# Revit family: CLEVER_GRIFERIA_GRIFO MURAL JARDÍN
name_source: partatom
category: Aparatos sanitarios
revit_build: Autodesk Revit 2016 (Build: 20151007_0715(x64)
units: mm (PartAtom-declared; Revit-internal decimal feet)

## family parameters
Anfitrión = Cara
Compartido = No
Corte con vacíos al cargar = No
Cota de conector redondo = Diámetro de uso
Número OmniClass = 23.45.05.14.14
Punto de cálculo de habitación = No
Tipo de pieza = Normal
Título OmniClass = Sinks/Lavatories

## types (1)
- Grifos individuales - Grifo mural jardín
    Altura = 100 mm  [stored 0.328084 ft]
    Apertura = Monomando
    BIMETRICAL = http://www.bimetrical.com
    BIMETRICAL Category = SanitaryTerminal
    Caudal AFS CTE = 0.2 L/s
    Certificaciones = -
    Conexión = Macho (1/2'')
    Conexión de residuos = No
    Conexión de ventilación = No
    Creado por = BIMETRICAL
    Código = 96133
    DN = 15  [stored 0.0492126 ft]
    DN (pulgadas) = 1/2''
    Descripción = Grifo mural jardin
    Elevación por defecto = 1219 mm
    Fabricante = CLEVER
    Fecha de Revisión = 03/2019
    Gama = CLEVER COLECTIVIDADES
    IfcExportAs = IfcSanitaryTerminalType
    IfcExportType = SINK
    Instalación = Pared
    Longitud caño = 82 mm  [stored 0.269029 ft]
    Marca = GRIFOS INDIVIDUALES
    Material cuerpo = CLEVER_Latón_Cromado
    Material maneta = CLEVER_Zamak_Cromado
    Material principal = CLEVER_Latón_Cromado
    Modelo = Grifos individuales - Grifo mural jardín
    Norma = -
    Presión = 1 - 10 bar (MAX. REC. 5 bar)
    Referencia Producto = 96133
    Serie = GRIFOS INDIVIDUALES
    URL = https://www.griferiaclever.com
    Versión Familia = 1.0
    Versión Revit = Revit 2016 - Español

note: [stored X ft] marks values corroborated as IEEE doubles in the binary element streams (Revit-internal decimal feet)

## geometry (parser evidence)
native form markers: Blend x4
no freeform markers — native parametric forms only
